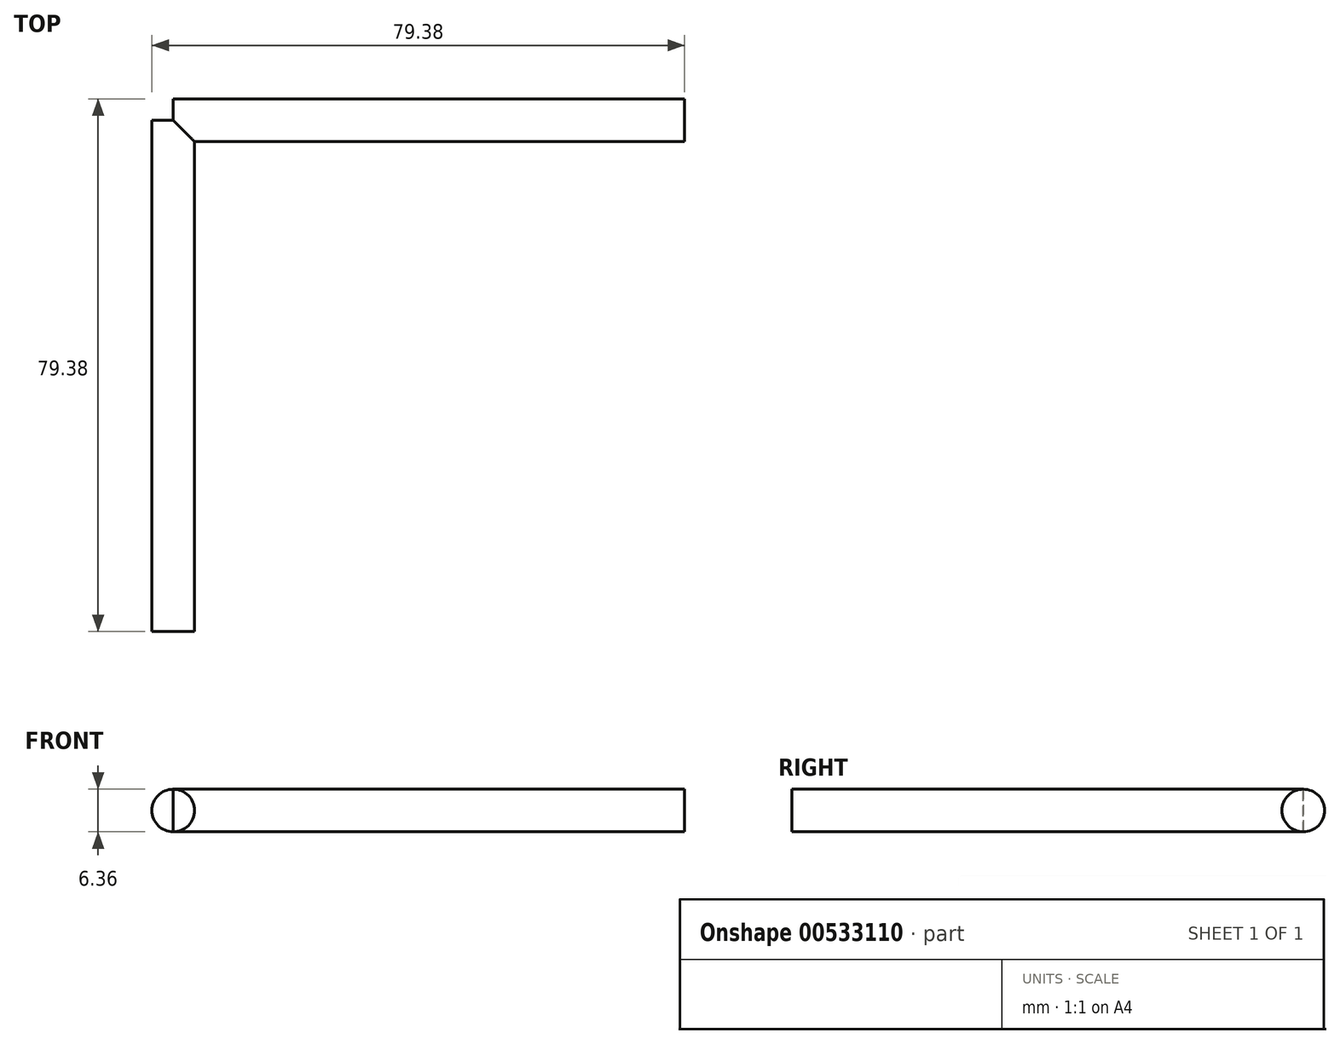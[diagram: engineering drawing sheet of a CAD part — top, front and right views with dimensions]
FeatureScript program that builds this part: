
annotation { "Feature Type Name" : "Feature", "Feature Type Description" : "" }
export const myFeature = defineFeature(function(context is Context, id is Id, definition is map)
    precondition{}
    {
        {
            var Q0;
            Q0=qCreatedBy(makeId("Front.planeOp"),FACE);
            var sketch = newSketch(context, id + "F0", { "sketchPlane" : qUnion([Q0])});
            skCircle(sketch, "E0", {"center": v(0, 0) * mm, "radius": 3.18 * mm});
            skSolve(sketch);
        }
        {
            var Q0;
            Q0 = qSketchRegion(id + "F0", true);
            extrude(context, id + "F1", {"entities" : qUnion([Q0]), "depth" : 76.2 * mm, "offsetDistance" : 25.4 * mm});
        }
        {
            var Q0;
            Q0=qCreatedBy(makeId("Right.planeOp"),FACE);
            var sketch = newSketch(context, id + "F2", { "sketchPlane" : qUnion([Q0])});
            skCircle(sketch, "E1", {"center": v(0, 0) * mm, "radius": 3.18 * mm});
            skSolve(sketch);
        }
        {
            var Q0;
            Q0 = qSketchRegion(id + "F2", true);
            extrude(context, id + "F3", {"entities" : qUnion([Q0]), "operationType" : NewBodyOperationType.ADD, "depth" : 25.4 * mm, "offsetDistance" : 25.4 * mm});
        }
        {
            var Q0;
            Q0=makeQuery(id+"F3.opExtrude","CAP_FACE",FACE,{"disambiguationData":[OSD([sQuery(id+"F2.wireOp",EDGE,"E1")])],"isStart":false});
            extrude(context, id + "F4", {"entities" : qUnion([Q0]), "operationType" : NewBodyOperationType.ADD, "depth" : 50.8 * mm, "offsetDistance" : 25.4 * mm});
        }
    });
